# Revit family: Gira_260565
name_source: partatom
category: Electrical Fixtures
revit_build: Autodesk Revit 2017 (Build: 20160225_1515(x64)
units: mm (PartAtom-declared; Revit-internal decimal feet)

## family parameters
Cut with Voids When Loaded = No
Host = Face
Maintain Annotation Orientation = Yes
Part Type = Normal
Room Calculation Point = No
Round Connector Dimension = Use Diameter
Shared = No

## types (1)
- Gira Keyless In keypad Gira TX_44 (WP FM) c.alum.
    Available = No
    BIM (1) = https://media.stage.bim.site und Tasten.rfa?public/gira/36a6b08/TX44_Komplettgerät_Schalten und Tasten.rfa
    Bus connection included = Yes
    Bus system KNX = No
    Bus system KNX radio = No
    Bus system LON = No
    Bus system Powernet = No
    Bus system radio frequent = No
    Category = Access control unit for bus system
    Data sheet (1) = https://katalog.gira.de
    Default Elevation = 1219 mm
    Description = Gira Keyless In keypad TX_44 CAl,Gira Keyless In keypad,,colour aluminium,Features:,- Installation in a device box.,- Stand-alone device or in combination with the Gira door communication system.,- For stand-alone operation, the integrated zero-voltage relay contacts are used for switching actions, e.g. for a door opener with its own power supply (e.g. common doorbell transformer).,- Start-up with direct configuration without a PC or programming software.,Inputs and outputs:,- Switching contact: Two relays with zero-voltage 2-way switch contacts, load capacity AC DC 24 V   1.6 A.,- Two connections for power supply.,- Keypad as an access control system with a capacitive and therefore wear-free button field.,- Frequently used number combinations cannot be recognised.,- Stand-alone device or in combination with the Gira door communication system as a door call system for buildings with several residential units.,- Special button C": Deleting an incorrect entry.,- Special button "Key": Direct door opening when the correct code has been entered.,- Special button "Bell": Specific selection of home stations in large facilities.,- Special button "F": Switching functions with switching actuators of the Gira door communication system.,- Homogeneous blue LED illumination of the numbers and special characters at night.,- Master PIN number provided on included sealed safety card if Administrator PIN number is lost.,- The keypad can manage up to 255 codes.,- Up to 32-digit codes are possible.,- Audible feedback when button is pressed.,- Three-colour LED status display during programming and operation.,- Warning tone in case of unauthorised removal of the keypad top unit for tamper detection. Tampering circuit with switching actuator in the Gira door communication system.,- The two integrated 2--way switch relays can be assigned two different codes, e.g. Code 1: door opening, Code 2: switching outdoor light.,Inputs and outputs:,- Connection cable connector strip for the Gira door communication system.,,Notes :,- Keyless In devices can be connected to the Gira HomeServer using the DCS-IP gateway. This enables intelligent links. In this way, e.g. temporary or one-time access authorisation can be easily granted. All data including access authorisations can be managed centrally and flexibly using the Gira HomeServer.,- Integration possible in Profile 55."
    GTIN = 4010337051411
    HAN = 260565
    HeinzeBIM = https://bimportal.heinze.de
    Manufacturer = Gira
    Manufacturer URL = https://www.gira.de
    Model = Code lock
    Name = Gira Keyless In keypad Gira TX_44 (WP FM) c.alum.
    Other bus systems = Other
    Transparent = No
    URL = http://katalog.gira.de

## geometry (parser evidence)
native form markers: Blend x2, Sweep x3
no freeform markers — native parametric forms only
